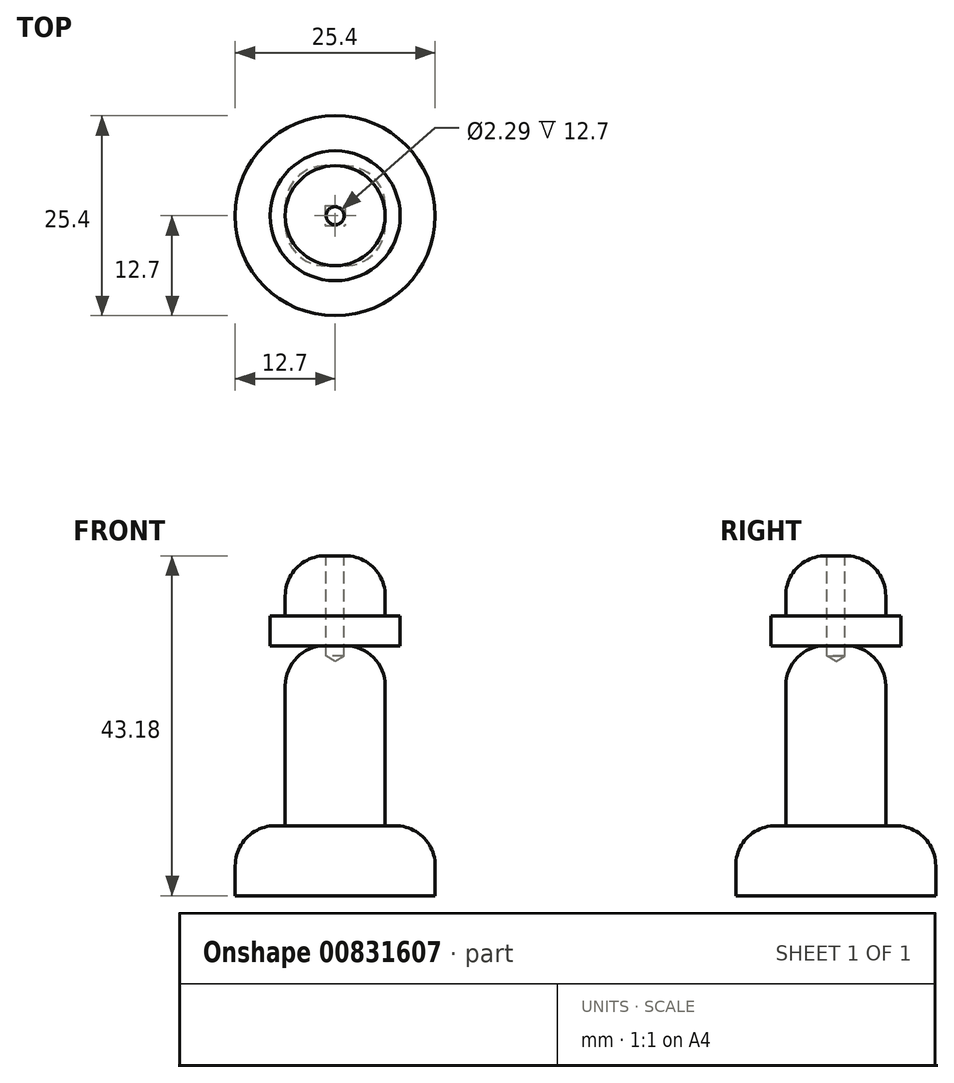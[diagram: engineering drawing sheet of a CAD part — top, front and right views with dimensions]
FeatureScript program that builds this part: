
annotation { "Feature Type Name" : "Feature", "Feature Type Description" : "" }
export const myFeature = defineFeature(function(context is Context, id is Id, definition is map)
    precondition{}
    {
        {
            var Q0;
            Q0=qCreatedBy(makeId("Top.planeOp"),FACE);
            var sketch = newSketch(context, id + "F0", { "sketchPlane" : qUnion([Q0])});
            skCircle(sketch, "E0", {"center": v(0, 0) * mm, "radius": 12.7 * mm});
            skSolve(sketch);
        }
        {
            var Q0;
            Q0 = qSketchRegion(id + "F0", true);
            extrude(context, id + "F1", {"entities" : qUnion([Q0]), "depth" : 8.9 * mm, "offsetDistance" : 25.4 * mm});
        }
        {
            var Q0;
            Q0=qCreatedBy(makeId("Top.planeOp"),FACE);
            var sketch = newSketch(context, id + "F2", { "sketchPlane" : qUnion([Q0])});
            skLineSegment(sketch, "E1.bottom", {"start": v(-6.35, 6.35) * mm, "end": v(6.35, 6.35) * mm});
            skLineSegment(sketch, "E1.top", {"start": v(-6.35, -6.35) * mm, "end": v(6.35, -6.35) * mm});
            skLineSegment(sketch, "E1.left", {"start": v(-6.35, 6.35) * mm, "end": v(-6.35, -6.35) * mm});
            skLineSegment(sketch, "E1.right", {"start": v(6.35, 6.35) * mm, "end": v(6.35, -6.35) * mm});
            skPoint(sketch, "E1.middle", {"position": v(0, 0) * mm});
            skSolve(sketch);
        }
        {
            var Q0;
            Q0 = qSketchRegion(id + "F2", true);
            extrude(context, id + "F3", {"entities" : qUnion([Q0]), "operationType" : NewBodyOperationType.ADD, "depth" : 31.75 * mm, "offsetDistance" : 25.4 * mm});
        }
        {
            var Q0;
            Q0=makeQuery(id+"F3.opExtrude","CAP_EDGE",EDGE,{"disambiguationData":[OSD([sQuery(id+"F2.wireOp",EDGE,"E1.right")])],"isStart":false});
            var Q1;
            Q1=makeQuery(id+"F3.opExtrude","CAP_EDGE",EDGE,{"disambiguationData":[OSD([sQuery(id+"F2.wireOp",EDGE,"E1.top")])],"isStart":false});
            var Q2;
            Q2=makeQuery(id+"F3.opExtrude","CAP_EDGE",EDGE,{"disambiguationData":[OSD([sQuery(id+"F2.wireOp",EDGE,"E1.left")])],"isStart":false});
            var Q3;
            Q3=makeQuery(id+"F3.opExtrude","CAP_EDGE",EDGE,{"disambiguationData":[OSD([sQuery(id+"F2.wireOp",EDGE,"E1.bottom")])],"isStart":false});
            fillet(context, id + "F4", {"entities" : qUnion([Q0, Q1, Q2, Q3]), "radius" : 5.08 * mm, "tangentPropagation" : true, "allowEdgeOverflow" : false});
        }
        {
            var Q0;
            Q0=makeQuery(id+"F3.opExtrude","SWEPT_EDGE",EDGE,{"disambiguationData":[OSD([sQuery(id+"F2.wireOp",EDGE,"E1.top"),sQuery(id+"F2.wireOp",EDGE,"E1.right")])]});
            var Q1;
            Q1=makeQuery(id+"F3.opExtrude","SWEPT_EDGE",EDGE,{"disambiguationData":[OSD([sQuery(id+"F2.wireOp",EDGE,"E1.top"),sQuery(id+"F2.wireOp",EDGE,"E1.left")])]});
            var Q2;
            Q2=makeQuery(id+"F3.opExtrude","SWEPT_EDGE",EDGE,{"disambiguationData":[OSD([sQuery(id+"F2.wireOp",EDGE,"E1.bottom"),sQuery(id+"F2.wireOp",EDGE,"E1.left")])]});
            var Q3;
            Q3=makeQuery(id+"F3.opExtrude","SWEPT_EDGE",EDGE,{"disambiguationData":[OSD([sQuery(id+"F2.wireOp",EDGE,"E1.bottom"),sQuery(id+"F2.wireOp",EDGE,"E1.right")])]});
            fillet(context, id + "F5", {"entities" : qUnion([Q0, Q1, Q2, Q3]), "radius" : 5.08 * mm, "tangentPropagation" : true, "allowEdgeOverflow" : false});
        }
        {
            var Q0;
            Q0=makeQuery(id+"F3.opExtrude","CAP_FACE",FACE,{"disambiguationData":[OSD([sQuery(id+"F2.wireOp",EDGE,"E1.bottom"),sQuery(id+"F2.wireOp",EDGE,"E1.top"),sQuery(id+"F2.wireOp",EDGE,"E1.left"),sQuery(id+"F2.wireOp",EDGE,"E1.right")])],"isStart":false});
            var sketch = newSketch(context, id + "F6", { "sketchPlane" : qUnion([Q0])});
            skCircle(sketch, "E2", {"center": v(0, 0) * mm, "radius": 8.26 * mm});
            skSolve(sketch);
        }
        {
            var Q0;
            Q0 = qSketchRegion(id + "F6", true);
            extrude(context, id + "F7", {"entities" : qUnion([Q0]), "operationType" : NewBodyOperationType.ADD, "depth" : 3.8 * mm, "offsetDistance" : 25.4 * mm});
        }
        {
            var Q0;
            Q0=makeQuery(id+"F7.opExtrude","CAP_FACE",FACE,{"disambiguationData":[OSD([sQuery(id+"F6.wireOp",EDGE,"E2")])],"isStart":false});
            var sketch = newSketch(context, id + "F8", { "sketchPlane" : qUnion([Q0])});
            skCircle(sketch, "E3", {"center": v(0, 0) * mm, "radius": 6.35 * mm});
            skSolve(sketch);
        }
        {
            var Q0;
            Q0 = qSketchRegion(id + "F8", true);
            extrude(context, id + "F9", {"entities" : qUnion([Q0]), "operationType" : NewBodyOperationType.ADD, "depth" : 7.62 * mm, "offsetDistance" : 25.4 * mm});
        }
        {
            var Q0;
            Q0=makeQuery(id+"F9.opExtrude","CAP_FACE",FACE,{"disambiguationData":[OSD([sQuery(id+"F8.wireOp",EDGE,"E3")])],"isStart":false});
            fillet(context, id + "F10", {"entities" : qUnion([Q0]), "radius" : 5.08 * mm, "tangentPropagation" : true, "allowEdgeOverflow" : false});
        }
        {
            var Q0;
            Q0=makeQuery(id+"F9.opExtrude","CAP_FACE",FACE,{"disambiguationData":[OSD([sQuery(id+"F8.wireOp",EDGE,"E3")])],"isStart":false});
            var sketch = newSketch(context, id + "F11", { "sketchPlane" : qUnion([Q0])});
            skPoint(sketch, "E4", {"position": v(0, 0) * mm});
            skSolve(sketch);
        }
        {
            var Q0;
            Q0=sQuery(id+"F11.wireOp",VERTEX,"E4");
            var Q1;
            Q1=makeQuery(id+"F1.opExtrude","SWEPT_BODY",BODY,{"disambiguationData":[OSD([sQuery(id+"F0.wireOp",EDGE,"E0")])]});
            hole(context, id + "F12", {"style" : HoleStyle.SIMPLE, "endStyle" : HoleEndStyle.BLIND, "holeDiameter" : 2.3 * mm, "majorDiameter" : 6.35 * mm, "holeDepth" : 12.7 * mm, "isTappedThrough" : true, "tappedDepth" : 12.7 * mm, "tapClearance" : 3, "locations" : qUnion([Q0]), "scope" : qUnion([Q1])});
        }
        {
            var Q0;
            Q0=makeQuery(id+"F1.opExtrude","CAP_EDGE",EDGE,{"disambiguationData":[OSD([sQuery(id+"F0.wireOp",EDGE,"E0")])],"isStart":false});
            fillet(context, id + "F13", {"entities" : qUnion([Q0]), "radius" : 5.08 * mm, "tangentPropagation" : true, "allowEdgeOverflow" : false});
        }
    });
